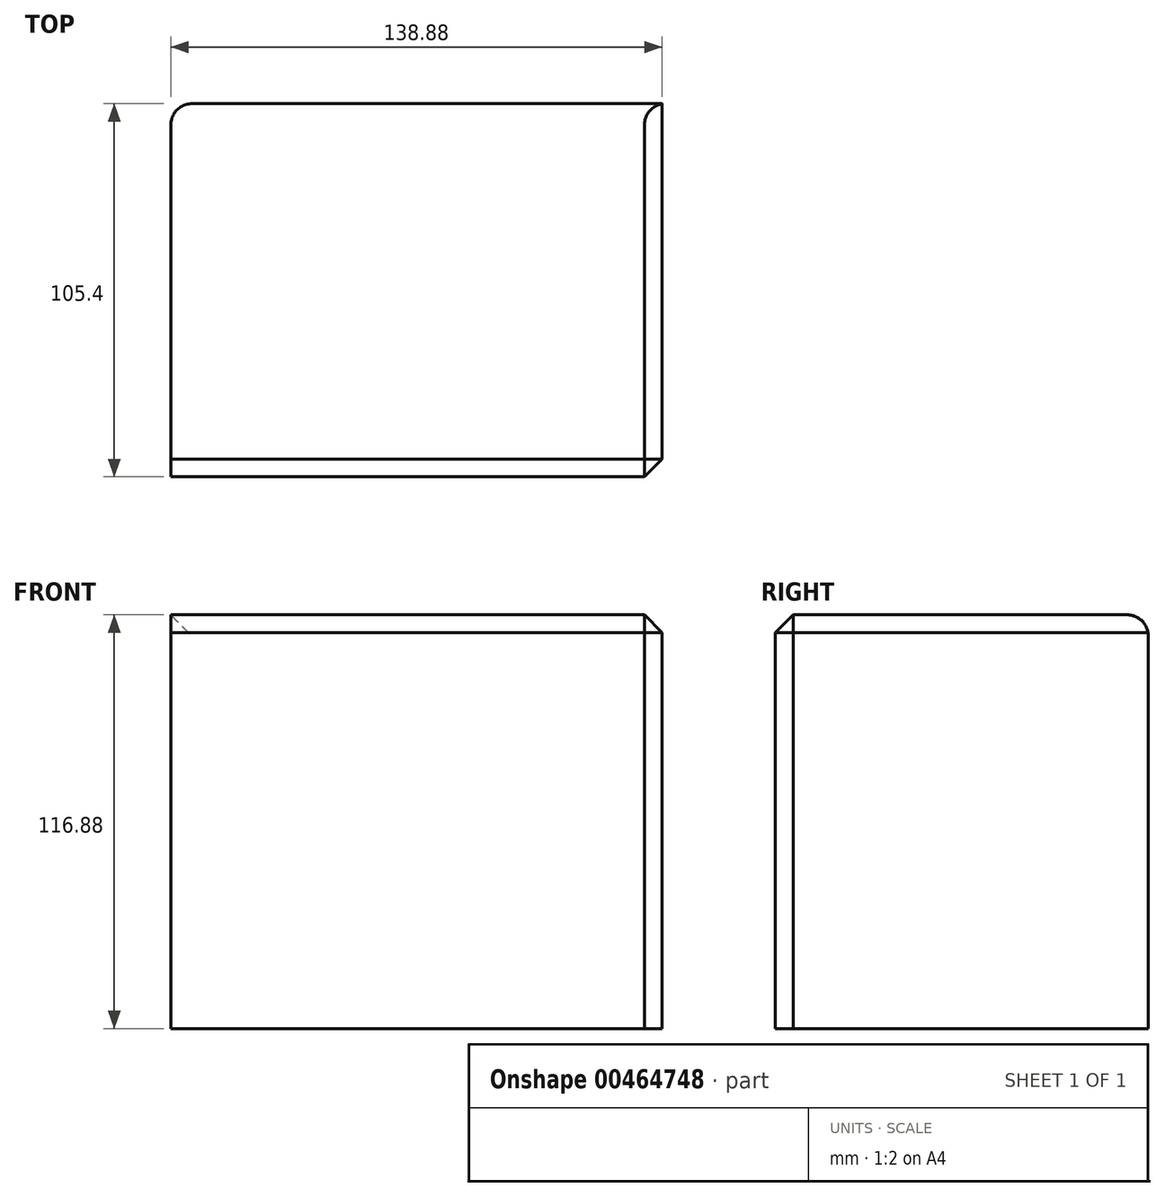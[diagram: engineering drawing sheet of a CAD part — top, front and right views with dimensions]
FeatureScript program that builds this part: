
annotation { "Feature Type Name" : "Feature", "Feature Type Description" : "" }
export const myFeature = defineFeature(function(context is Context, id is Id, definition is map)
    precondition{}
    {
        {
            var Q0;
            Q0=qCreatedBy(makeId("Front.planeOp"),FACE);
            var sketch = newSketch(context, id + "F0", { "sketchPlane" : qUnion([Q0])});
            skLineSegment(sketch, "E0.bottom", {"start": v(69.44, 58.44) * mm, "end": v(-69.44, 58.44) * mm});
            skLineSegment(sketch, "E0.top", {"start": v(69.44, -58.44) * mm, "end": v(-69.44, -58.44) * mm});
            skLineSegment(sketch, "E0.left", {"start": v(69.44, 58.44) * mm, "end": v(69.44, -58.44) * mm});
            skLineSegment(sketch, "E0.right", {"start": v(-69.44, 58.44) * mm, "end": v(-69.44, -58.44) * mm});
            skPoint(sketch, "E0.middle", {"position": v(0, 0) * mm});
            skSolve(sketch);
        }
        {
            var Q0;
            Q0=makeQuery(id+"F0.imprint","IMPRINT",FACE,{"disambiguationData":[TD([[makeQuery(id+"F0.imprint","IMPRINT",EDGE,{"derivedFrom":sQuery(id+"F0.wireOp",EDGE,"E0.bottom")}),1.0]])]});
            extrude(context, id + "F1", {"entities" : qUnion([Q0]), "depth" : 105.4 * mm});
        }
        {
            var Q0;
            Q0=makeQuery(id+"F1.opExtrude","SWEPT_EDGE",EDGE,{"disambiguationData":[OSD([sQuery(id+"F0.wireOp",EDGE,"E0.bottom"),sQuery(id+"F0.wireOp",EDGE,"E0.left")])]});
            var Q1;
            Q1=makeQuery(id+"F1.opExtrude","CAP_EDGE",EDGE,{"disambiguationData":[OSD([sQuery(id+"F0.wireOp",EDGE,"E0.bottom")])],"isStart":false});
            var Q2;
            Q2=makeQuery(id+"F1.opExtrude","CAP_EDGE",EDGE,{"disambiguationData":[OSD([sQuery(id+"F0.wireOp",EDGE,"E0.left")])],"isStart":false});
            chamfer(context, id + "F2", {"entities" : qUnion([Q0, Q1, Q2]), "width" : 5 * mm, "tangentPropagation" : true});
        }
        {
            var Q0;
            Q0=makeQuery(id+"F1.opExtrude","CAP_EDGE",EDGE,{"disambiguationData":[OSD([sQuery(id+"F0.wireOp",EDGE,"E0.right")])],"isStart":true});
            var Q1;
            Q1=makeQuery(id+"F1.opExtrude","CAP_EDGE",EDGE,{"disambiguationData":[OSD([sQuery(id+"F0.wireOp",EDGE,"E0.bottom")])],"isStart":true});
            fillet(context, id + "F3", {"entities" : qUnion([Q0, Q1]), "radius" : 6 * mm, "tangentPropagation" : true, "allowEdgeOverflow" : false});
        }
    });
